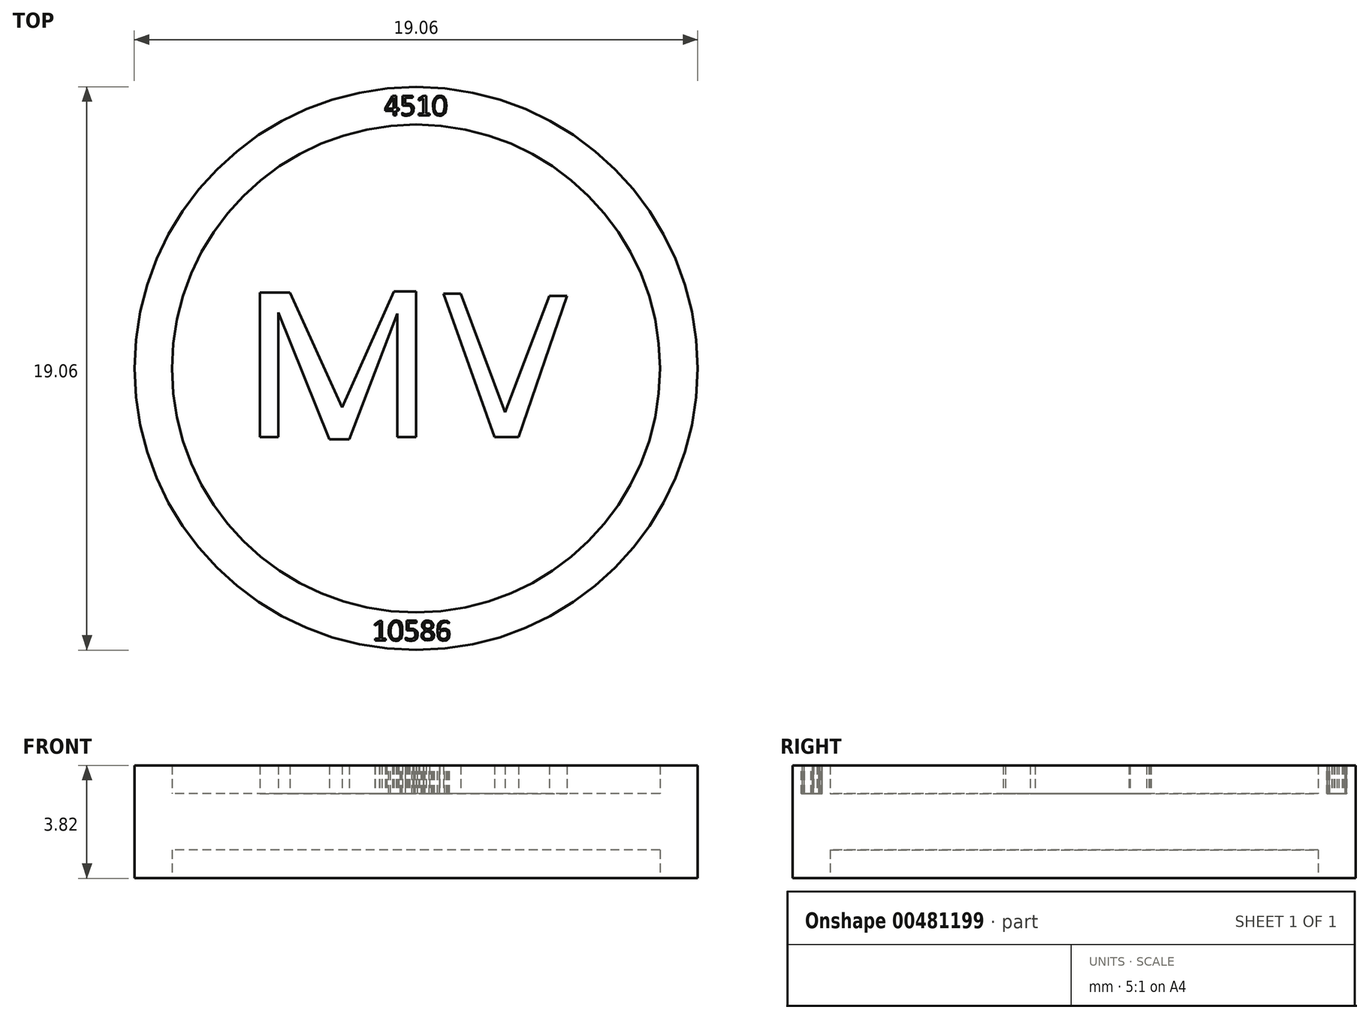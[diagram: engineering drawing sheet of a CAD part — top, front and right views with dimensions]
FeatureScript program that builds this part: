
annotation { "Feature Type Name" : "Feature", "Feature Type Description" : "" }
export const myFeature = defineFeature(function(context is Context, id is Id, definition is map)
    precondition{}
    {
        {
            var Q0;
            Q0=qCreatedBy(makeId("Top.planeOp"),FACE);
            var sketch = newSketch(context, id + "F0", { "sketchPlane" : qUnion([Q0])});
            skCircle(sketch, "E0", {"center": v(0, 0) * mm, "radius": 9.53 * mm});
            skCircle(sketch, "E1", {"center": v(0, 0) * mm, "radius": 8.26 * mm});
            skLineSegment(sketch, "E2", {"start": v(-5.28, -2.32) * mm, "end": v(-4.66, -2.32) * mm});
            skLineSegment(sketch, "E3", {"start": v(-4.66, -2.32) * mm, "end": v(-4.66, 1.9) * mm});
            skLineSegment(sketch, "E4", {"start": v(-4.66, 1.9) * mm, "end": v(-2.94, -2.39) * mm});
            skLineSegment(sketch, "E5", {"start": v(-2.94, -2.39) * mm, "end": v(-2.25, -2.39) * mm});
            skLineSegment(sketch, "E6", {"start": v(-2.25, -2.39) * mm, "end": v(-0.64, 1.86) * mm});
            skLineSegment(sketch, "E7", {"start": v(-0.64, 1.86) * mm, "end": v(-0.64, -2.32) * mm});
            skLineSegment(sketch, "E8", {"start": v(-0.64, -2.32) * mm, "end": v(0, -2.32) * mm});
            skLineSegment(sketch, "E9", {"start": v(0, -2.32) * mm, "end": v(0, 2.61) * mm});
            skLineSegment(sketch, "E10", {"start": v(0, 2.61) * mm, "end": v(-0.74, 2.61) * mm});
            skLineSegment(sketch, "E11", {"start": v(-0.74, 2.61) * mm, "end": v(-2.5, -1.31) * mm});
            skLineSegment(sketch, "E12", {"start": v(-2.5, -1.31) * mm, "end": v(-4.27, 2.57) * mm});
            skLineSegment(sketch, "E13", {"start": v(-4.27, 2.57) * mm, "end": v(-5.1, 2.57) * mm});
            skLineSegment(sketch, "E14", {"start": v(-5.28, -2.32) * mm, "end": v(-5.28, 2.57) * mm});
            skLineSegment(sketch, "E15", {"start": v(-5.28, 2.57) * mm, "end": v(-5.1, 2.57) * mm});
            skLineSegment(sketch, "E16", {"start": v(0.93, 2.53) * mm, "end": v(1.52, 2.53) * mm});
            skLineSegment(sketch, "E17", {"start": v(1.52, 2.53) * mm, "end": v(3.02, -1.48) * mm});
            skLineSegment(sketch, "E18", {"start": v(3.02, -1.48) * mm, "end": v(4.51, 2.46) * mm});
            skLineSegment(sketch, "E19", {"start": v(4.51, 2.46) * mm, "end": v(5.1, 2.46) * mm});
            skLineSegment(sketch, "E20", {"start": v(5.1, 2.46) * mm, "end": v(3.47, -2.32) * mm});
            skLineSegment(sketch, "E21", {"start": v(3.47, -2.32) * mm, "end": v(2.65, -2.32) * mm});
            skLineSegment(sketch, "E22", {"start": v(2.65, -2.32) * mm, "end": v(0.93, 2.53) * mm});
            skLineSegment(sketch, "E23", {"start": v(-0.8, 9.23) * mm, "end": v(-0.67, 9.23) * mm});
            skLineSegment(sketch, "E24", {"start": v(-0.67, 9.23) * mm, "end": v(-0.67, 8.8) * mm});
            skLineSegment(sketch, "E25", {"start": v(-0.67, 8.8) * mm, "end": v(-0.59, 8.8) * mm});
            skLineSegment(sketch, "E26", {"start": v(-0.59, 8.8) * mm, "end": v(-0.59, 8.73) * mm});
            skLineSegment(sketch, "E27", {"start": v(-0.59, 8.73) * mm, "end": v(-0.67, 8.73) * mm});
            skLineSegment(sketch, "E28", {"start": v(-0.67, 8.73) * mm, "end": v(-0.67, 8.56) * mm});
            skLineSegment(sketch, "E29", {"start": v(-0.67, 8.56) * mm, "end": v(-0.75, 8.56) * mm});
            skLineSegment(sketch, "E30", {"start": v(-0.75, 8.56) * mm, "end": v(-0.75, 8.72) * mm});
            skLineSegment(sketch, "E31", {"start": v(-0.75, 8.72) * mm, "end": v(-1.04, 8.72) * mm});
            skLineSegment(sketch, "E32", {"start": v(-1.04, 8.72) * mm, "end": v(-1.04, 8.8) * mm});
            skLineSegment(sketch, "E33", {"start": v(-1.04, 8.8) * mm, "end": v(-0.8, 9.23) * mm});
            skLineSegment(sketch, "E34", {"start": v(-0.45, 9.23) * mm, "end": v(-0.45, 8.9) * mm});
            skLineSegment(sketch, "E35", {"start": v(-0.45, 8.9) * mm, "end": v(-0.27, 8.9) * mm});
            skLineSegment(sketch, "E36", {"start": v(-0.45, 9.23) * mm, "end": v(-0.12, 9.23) * mm});
            skLineSegment(sketch, "E37", {"start": v(-0.12, 9.23) * mm, "end": v(-0.12, 9.16) * mm});
            skLineSegment(sketch, "E38", {"start": v(-0.12, 9.16) * mm, "end": v(-0.37, 9.16) * mm});
            skLineSegment(sketch, "E39", {"start": v(-0.37, 9.16) * mm, "end": v(-0.37, 8.96) * mm});
            skLineSegment(sketch, "E40", {"start": v(-0.37, 8.96) * mm, "end": v(-0.21, 8.96) * mm});
            skFitSpline(sketch, "E41", {"points": [v(-0.27, 8.9) * mm, v(-0.2, 8.88) * mm, v(-0.15, 8.81) * mm, v(-0.16, 8.67) * mm, v(-0.27, 8.61) * mm, v(-0.41, 8.62) * mm, v(-0.46, 8.65) * mm, v(-0.47, 8.62) * mm, v(-0.43, 8.57) * mm, v(-0.24, 8.56) * mm, v(-0.17, 8.59) * mm, v(-0.13, 8.62) * mm, v(-0.08, 8.74) * mm, v(-0.1, 8.88) * mm, v(-0.21, 8.96) * mm], "startDerivative": vector(0.63, -0.29) * mm, "endDerivative": vector(-1.44, 0.73) * mm});
            skLineSegment(sketch, "E42", {"start": v(0.11, 9.07) * mm, "end": v(0.25, 9.14) * mm});
            skLineSegment(sketch, "E43", {"start": v(0.25, 9.14) * mm, "end": v(0.25, 8.62) * mm});
            skLineSegment(sketch, "E44", {"start": v(0.25, 8.62) * mm, "end": v(0.1, 8.62) * mm});
            skLineSegment(sketch, "E45", {"start": v(0.1, 8.62) * mm, "end": v(0.1, 8.56) * mm});
            skLineSegment(sketch, "E46", {"start": v(0.1, 8.56) * mm, "end": v(0.46, 8.56) * mm});
            skLineSegment(sketch, "E47", {"start": v(0.46, 8.56) * mm, "end": v(0.46, 8.62) * mm});
            skLineSegment(sketch, "E48", {"start": v(0.46, 8.62) * mm, "end": v(0.34, 8.62) * mm});
            skLineSegment(sketch, "E49", {"start": v(0.34, 8.62) * mm, "end": v(0.34, 9.23) * mm});
            skLineSegment(sketch, "E50", {"start": v(0.34, 9.23) * mm, "end": v(0.26, 9.23) * mm});
            skLineSegment(sketch, "E51", {"start": v(0.26, 9.23) * mm, "end": v(0.1, 9.12) * mm});
            skLineSegment(sketch, "E52", {"start": v(0.1, 9.12) * mm, "end": v(0.1, 9.07) * mm});
            skLineSegment(sketch, "E53", {"start": v(0.1, 9.07) * mm, "end": v(0.11, 9.07) * mm});
            skFitSpline(sketch, "E54", {"points": [v(0.8, 9.17) * mm, v(0.87, 9.17) * mm, v(0.93, 9.09) * mm, v(0.96, 8.96) * mm, v(0.96, 8.8) * mm, v(0.94, 8.68) * mm, v(0.88, 8.62) * mm, v(0.77, 8.61) * mm, v(0.7, 8.63) * mm, v(0.64, 8.75) * mm, v(0.64, 9.01) * mm, v(0.7, 9.13) * mm, v(0.8, 9.17) * mm], "startDerivative": vector(1.02, 0.3) * mm, "endDerivative": vector(1.6, 0.29) * mm});
            skFitSpline(sketch, "E55", {"points": [v(0.8, 9.17) * mm, v(0.8, 9.17) * mm], "startDerivative": vector(0, 0) * mm, "endDerivative": vector(0, 0) * mm});
            skFitSpline(sketch, "E56", {"points": [v(0.8, 9.23) * mm, v(0.9, 9.21) * mm, v(0.98, 9.12) * mm, v(1.02, 8.97) * mm, v(1.01, 8.72) * mm, v(0.94, 8.61) * mm, v(0.85, 8.55) * mm, v(0.7, 8.57) * mm, v(0.6, 8.7) * mm, v(0.57, 8.93) * mm, v(0.62, 9.1) * mm, v(0.72, 9.2) * mm, v(0.8, 9.23) * mm]});
            skLineSegment(sketch, "E57", {"start": v(-0.76, 9.16) * mm, "end": v(-0.76, 8.8) * mm});
            skLineSegment(sketch, "E58", {"start": v(-0.76, 8.8) * mm, "end": v(-1, 8.8) * mm});
            skLineSegment(sketch, "E59", {"start": v(-1, 8.8) * mm, "end": v(-1, 8.82) * mm});
            skLineSegment(sketch, "E60", {"start": v(-1, 8.82) * mm, "end": v(-0.76, 9.16) * mm});
            skLineSegment(sketch, "E61", {"start": v(-1.24, -8.55) * mm, "end": v(-1.4, -8.65) * mm});
            skLineSegment(sketch, "E62", {"start": v(-1.4, -8.65) * mm, "end": v(-1.4, -8.7) * mm});
            skLineSegment(sketch, "E63", {"start": v(-1.4, -8.7) * mm, "end": v(-1.24, -8.6) * mm});
            skLineSegment(sketch, "E64", {"start": v(-1.24, -8.6) * mm, "end": v(-1.24, -9.14) * mm});
            skLineSegment(sketch, "E65", {"start": v(-1.24, -9.14) * mm, "end": v(-1.39, -9.14) * mm});
            skLineSegment(sketch, "E66", {"start": v(-1.39, -9.14) * mm, "end": v(-1.39, -9.2) * mm});
            skLineSegment(sketch, "E67", {"start": v(-1.39, -9.2) * mm, "end": v(-1.02, -9.2) * mm});
            skLineSegment(sketch, "E68", {"start": v(-1.02, -9.2) * mm, "end": v(-1.02, -9.14) * mm});
            skLineSegment(sketch, "E69", {"start": v(-1.02, -9.14) * mm, "end": v(-1.16, -9.14) * mm});
            skLineSegment(sketch, "E70", {"start": v(-1.16, -9.14) * mm, "end": v(-1.16, -8.54) * mm});
            skLineSegment(sketch, "E71", {"start": v(-1.16, -8.54) * mm, "end": v(-1.24, -8.55) * mm});
            skFitSpline(sketch, "E72", {"points": [v(-0.7, -8.59) * mm, v(-0.62, -8.6) * mm, v(-0.56, -8.69) * mm, v(-0.55, -9.07) * mm, v(-0.63, -9.14) * mm, v(-0.76, -9.15) * mm, v(-0.85, -8.99) * mm, v(-0.83, -8.7) * mm, v(-0.7, -8.59) * mm]});
            skFitSpline(sketch, "E73", {"points": [v(-0.73, -8.53) * mm, v(-0.6, -8.53) * mm, v(-0.5, -8.64) * mm, v(-0.47, -8.84) * mm, v(-0.47, -9.04) * mm, v(-0.54, -9.15) * mm, v(-0.63, -9.21) * mm, v(-0.79, -9.2) * mm, v(-0.9, -9.01) * mm, v(-0.91, -8.75) * mm, v(-0.82, -8.59) * mm, v(-0.73, -8.53) * mm]});
            skLineSegment(sketch, "E74", {"start": v(-0.31, -8.53) * mm, "end": v(0.02, -8.53) * mm});
            skLineSegment(sketch, "E75", {"start": v(0.02, -8.53) * mm, "end": v(0.02, -8.6) * mm});
            skLineSegment(sketch, "E76", {"start": v(0.02, -8.6) * mm, "end": v(-0.25, -8.6) * mm});
            skLineSegment(sketch, "E77", {"start": v(-0.25, -8.6) * mm, "end": v(-0.25, -8.81) * mm});
            skLineSegment(sketch, "E78", {"start": v(-0.25, -8.81) * mm, "end": v(-0.07, -8.81) * mm});
            skLineSegment(sketch, "E79", {"start": v(-0.31, -8.53) * mm, "end": v(-0.31, -8.86) * mm});
            skLineSegment(sketch, "E80", {"start": v(-0.31, -8.86) * mm, "end": v(-0.1, -8.86) * mm});
            skFitSpline(sketch, "E81", {"points": [v(-0.1, -8.86) * mm, v(-0.06, -8.9) * mm, v(-0.03, -9.05) * mm, v(-0.1, -9.13) * mm, v(-0.27, -9.15) * mm, v(-0.34, -9.11) * mm, v(-0.36, -9.15) * mm, v(-0.3, -9.2) * mm, v(-0.07, -9.2) * mm, v(0.05, -9.07) * mm, v(0.03, -8.9) * mm, v(-0.07, -8.81) * mm], "startDerivative": vector(0.84, -0.23) * mm, "endDerivative": vector(-1.4, 0.64) * mm});
            skFitSpline(sketch, "E82", {"points": [v(0.34, -8.53) * mm, v(0.46, -8.54) * mm, v(0.55, -8.6) * mm, v(0.59, -8.68) * mm, v(0.57, -8.78) * mm, v(0.45, -8.85) * mm, v(0.57, -8.93) * mm, v(0.6, -9.12) * mm, v(0.51, -9.18) * mm, v(0.46, -9.2) * mm, v(0.3, -9.2) * mm, v(0.2, -9.13) * mm, v(0.19, -8.98) * mm, v(0.3, -8.85) * mm, v(0.2, -8.74) * mm, v(0.23, -8.6) * mm, v(0.34, -8.53) * mm]});
            skFitSpline(sketch, "E83", {"points": [v(0.35, -8.6) * mm, v(0.47, -8.6) * mm, v(0.52, -8.65) * mm, v(0.52, -8.74) * mm, v(0.47, -8.8) * mm, v(0.4, -8.81) * mm, v(0.34, -8.8) * mm, v(0.29, -8.75) * mm, v(0.28, -8.66) * mm, v(0.35, -8.6) * mm]});
            skFitSpline(sketch, "E84", {"points": [v(0.4, -8.9) * mm, v(0.46, -8.92) * mm, v(0.5, -8.96) * mm, v(0.53, -9.02) * mm, v(0.52, -9.1) * mm, v(0.48, -9.15) * mm, v(0.39, -9.15) * mm, v(0.3, -9.14) * mm, v(0.25, -9.09) * mm, v(0.25, -8.98) * mm, v(0.31, -8.91) * mm, v(0.4, -8.9) * mm]});
            skFitSpline(sketch, "E85", {"points": [v(1.1, -8.63) * mm, v(1.08, -8.6) * mm, v(1, -8.59) * mm, v(0.9, -8.6) * mm, v(0.84, -8.67) * mm, v(0.8, -8.74) * mm, v(0.8, -8.84) * mm, v(0.88, -8.82) * mm, v(1.03, -8.81) * mm, v(1.12, -8.88) * mm, v(1.12, -9.11) * mm, v(1.02, -9.2) * mm, v(0.86, -9.2) * mm, v(0.75, -9.1) * mm, v(0.74, -8.73) * mm, v(0.76, -8.65) * mm, v(0.85, -8.55) * mm, v(1, -8.53) * mm, v(1.1, -8.56) * mm, v(1.12, -8.63) * mm, v(1.1, -8.63) * mm]});
            skFitSpline(sketch, "E86", {"points": [v(0.93, -8.87) * mm, v(1, -8.87) * mm, v(1.05, -8.9) * mm, v(1.07, -8.97) * mm, v(1.07, -9.06) * mm, v(1.03, -9.12) * mm, v(0.98, -9.15) * mm, v(0.88, -9.14) * mm, v(0.8, -9.1) * mm, v(0.8, -8.98) * mm, v(0.84, -8.88) * mm, v(0.93, -8.87) * mm]});
            skSolve(sketch);
        }
        {
            var Q0;
            Q0=makeQuery(id+"F0.imprint","IMPRINT",FACE,{"disambiguationData":[TD([[makeQuery(id+"F0.imprint","IMPRINT",EDGE,{"derivedFrom":sQuery(id+"F0.wireOp",EDGE,"E0")}),1.0]])]});
            var Q1;
            Q1=makeQuery(id+"F0.imprint","IMPRINT",FACE,{"disambiguationData":[TD([[makeQuery(id+"F0.imprint","IMPRINT",EDGE,{"derivedFrom":sQuery(id+"F0.wireOp",EDGE,"E72")}),-1.0]])]});
            var Q2;
            Q2=makeQuery(id+"F0.imprint","IMPRINT",FACE,{"disambiguationData":[TD([[makeQuery(id+"F0.imprint","IMPRINT",EDGE,{"derivedFrom":sQuery(id+"F0.wireOp",EDGE,"E84")}),-1.0]])]});
            var Q3;
            Q3=makeQuery(id+"F0.imprint","IMPRINT",FACE,{"disambiguationData":[TD([[makeQuery(id+"F0.imprint","IMPRINT",EDGE,{"derivedFrom":sQuery(id+"F0.wireOp",EDGE,"E83")}),-1.0]])]});
            var Q4;
            Q4=makeQuery(id+"F0.imprint","IMPRINT",FACE,{"disambiguationData":[TD([[makeQuery(id+"F0.imprint","IMPRINT",EDGE,{"derivedFrom":sQuery(id+"F0.wireOp",EDGE,"E86")}),-1.0]])]});
            var Q5;
            Q5=makeQuery(id+"F0.imprint","IMPRINT",FACE,{"disambiguationData":[TD([[makeQuery(id+"F0.imprint","IMPRINT",EDGE,{"derivedFrom":sQuery(id+"F0.wireOp",EDGE,"E57")}),-1.0]])]});
            var Q6;
            Q6=makeQuery(id+"F0.imprint","IMPRINT",FACE,{"disambiguationData":[TD([[makeQuery(id+"F0.imprint","IMPRINT",EDGE,{"derivedFrom":sQuery(id+"F0.wireOp",EDGE,"E54")}),-1.0]])]});
            extrude(context, id + "F1", {"entities" : qUnion([Q0, Q1, Q2, Q3, Q4, Q5, Q6]), "endBound" : BoundingType.SYMMETRIC, "depth" : 3.8 * mm});
        }
        {
            var Q0;
            Q0=makeQuery(id+"F0.imprint","IMPRINT",FACE,{"disambiguationData":[TD([[makeQuery(id+"F0.imprint","IMPRINT",EDGE,{"derivedFrom":sQuery(id+"F0.wireOp",EDGE,"E1")}),1.0]])]});
            var Q1;
            Q1=makeQuery(id+"F0.imprint","IMPRINT",FACE,{"disambiguationData":[TD([[makeQuery(id+"F0.imprint","IMPRINT",EDGE,{"derivedFrom":sQuery(id+"F0.wireOp",EDGE,"E2")}),1.0]])]});
            var Q2;
            Q2=makeQuery(id+"F0.imprint","IMPRINT",FACE,{"disambiguationData":[TD([[makeQuery(id+"F0.imprint","IMPRINT",EDGE,{"derivedFrom":sQuery(id+"F0.wireOp",EDGE,"E16")}),-1.0]])]});
            extrude(context, id + "F2", {"entities" : qUnion([Q0, Q1, Q2]), "operationType" : NewBodyOperationType.ADD, "endBound" : BoundingType.SYMMETRIC, "depth" : 1.9 * mm});
        }
        {
            var Q0;
            Q0=makeQuery(id+"F0.imprint","IMPRINT",FACE,{"disambiguationData":[TD([[makeQuery(id+"F0.imprint","IMPRINT",EDGE,{"derivedFrom":sQuery(id+"F0.wireOp",EDGE,"E2")}),1.0]])]});
            var Q1;
            Q1=makeQuery(id+"F0.imprint","IMPRINT",FACE,{"disambiguationData":[TD([[makeQuery(id+"F0.imprint","IMPRINT",EDGE,{"derivedFrom":sQuery(id+"F0.wireOp",EDGE,"E16")}),-1.0]])]});
            extrude(context, id + "F3", {"entities" : qUnion([Q0, Q1]), "operationType" : NewBodyOperationType.ADD, "depth" : 1.9 * mm});
        }
        {
            var Q0;
            Q0=makeQuery(id+"F0.imprint","IMPRINT",FACE,{"disambiguationData":[TD([[makeQuery(id+"F0.imprint","IMPRINT",EDGE,{"derivedFrom":sQuery(id+"F0.wireOp",EDGE,"E61")}),1.0]])]});
            var Q1;
            Q1=makeQuery(id+"F0.imprint","IMPRINT",FACE,{"disambiguationData":[TD([[makeQuery(id+"F0.imprint","IMPRINT",EDGE,{"derivedFrom":sQuery(id+"F0.wireOp",EDGE,"E72")}),1.0]])]});
            var Q2;
            Q2=makeQuery(id+"F0.imprint","IMPRINT",FACE,{"disambiguationData":[TD([[makeQuery(id+"F0.imprint","IMPRINT",EDGE,{"derivedFrom":sQuery(id+"F0.wireOp",EDGE,"E74")}),-1.0]])]});
            var Q3;
            Q3=makeQuery(id+"F0.imprint","IMPRINT",FACE,{"disambiguationData":[TD([[makeQuery(id+"F0.imprint","IMPRINT",EDGE,{"derivedFrom":sQuery(id+"F0.wireOp",EDGE,"E82")}),-1.0]])]});
            var Q4;
            Q4=makeQuery(id+"F0.imprint","IMPRINT",FACE,{"disambiguationData":[TD([[makeQuery(id+"F0.imprint","IMPRINT",EDGE,{"derivedFrom":sQuery(id+"F0.wireOp",EDGE,"E23")}),-1.0]])]});
            var Q5;
            Q5=makeQuery(id+"F0.imprint","IMPRINT",FACE,{"disambiguationData":[TD([[makeQuery(id+"F0.imprint","IMPRINT",EDGE,{"derivedFrom":sQuery(id+"F0.wireOp",EDGE,"E34")}),1.0]])]});
            var Q6;
            Q6=makeQuery(id+"F0.imprint","IMPRINT",FACE,{"disambiguationData":[TD([[makeQuery(id+"F0.imprint","IMPRINT",EDGE,{"derivedFrom":sQuery(id+"F0.wireOp",EDGE,"E42")}),1.0]])]});
            var Q7;
            Q7=makeQuery(id+"F0.imprint","IMPRINT",FACE,{"disambiguationData":[TD([[makeQuery(id+"F0.imprint","IMPRINT",EDGE,{"derivedFrom":sQuery(id+"F0.wireOp",EDGE,"E54")}),1.0]])]});
            var Q8;
            Q8=makeQuery(id+"F0.imprint","IMPRINT",FACE,{"disambiguationData":[TD([[makeQuery(id+"F0.imprint","IMPRINT",EDGE,{"derivedFrom":sQuery(id+"F0.wireOp",EDGE,"E85")}),-1.0]])]});
            extrude(context, id + "F4", {"entities" : qUnion([Q0, Q1, Q2, Q3, Q4, Q5, Q6, Q7, Q8]), "endBound" : BoundingType.SYMMETRIC, "depth" : 1.9 * mm});
        }
        {
            var Q0;
            Q0=makeQuery(id+"F4.opExtrude","CAP_FACE",FACE,{"disambiguationData":[OSD([sQuery(id+"F0.wireOp",EDGE,"E23"),sQuery(id+"F0.wireOp",EDGE,"E24"),sQuery(id+"F0.wireOp",EDGE,"E25"),sQuery(id+"F0.wireOp",EDGE,"E26"),sQuery(id+"F0.wireOp",EDGE,"E27"),sQuery(id+"F0.wireOp",EDGE,"E28"),sQuery(id+"F0.wireOp",EDGE,"E29"),sQuery(id+"F0.wireOp",EDGE,"E30"),sQuery(id+"F0.wireOp",EDGE,"E31"),sQuery(id+"F0.wireOp",EDGE,"E32"),sQuery(id+"F0.wireOp",EDGE,"E33"),sQuery(id+"F0.wireOp",EDGE,"E57"),sQuery(id+"F0.wireOp",EDGE,"E58"),sQuery(id+"F0.wireOp",EDGE,"E59"),sQuery(id+"F0.wireOp",EDGE,"E60")])],"isStart":true});
            var Q1;
            Q1=makeQuery(id+"F4.opExtrude","CAP_FACE",FACE,{"disambiguationData":[OSD([sQuery(id+"F0.wireOp",EDGE,"E34"),sQuery(id+"F0.wireOp",EDGE,"E35"),sQuery(id+"F0.wireOp",EDGE,"E36"),sQuery(id+"F0.wireOp",EDGE,"E37"),sQuery(id+"F0.wireOp",EDGE,"E38"),sQuery(id+"F0.wireOp",EDGE,"E39"),sQuery(id+"F0.wireOp",EDGE,"E40"),sQuery(id+"F0.wireOp",EDGE,"E41")])],"isStart":true});
            var Q2;
            Q2=makeQuery(id+"F4.opExtrude","CAP_FACE",FACE,{"disambiguationData":[OSD([sQuery(id+"F0.wireOp",EDGE,"E42"),sQuery(id+"F0.wireOp",EDGE,"E43"),sQuery(id+"F0.wireOp",EDGE,"E44"),sQuery(id+"F0.wireOp",EDGE,"E45"),sQuery(id+"F0.wireOp",EDGE,"E46"),sQuery(id+"F0.wireOp",EDGE,"E47"),sQuery(id+"F0.wireOp",EDGE,"E48"),sQuery(id+"F0.wireOp",EDGE,"E49"),sQuery(id+"F0.wireOp",EDGE,"E50"),sQuery(id+"F0.wireOp",EDGE,"E51"),sQuery(id+"F0.wireOp",EDGE,"E52"),sQuery(id+"F0.wireOp",EDGE,"E53")])],"isStart":true});
            var Q3;
            Q3=makeQuery(id+"F4.opExtrude","CAP_FACE",FACE,{"disambiguationData":[OSD([sQuery(id+"F0.wireOp",EDGE,"E54"),sQuery(id+"F0.wireOp",EDGE,"E55"),sQuery(id+"F0.wireOp",EDGE,"E56")])],"isStart":true});
            var Q4;
            Q4=makeQuery(id+"F4.opExtrude","CAP_FACE",FACE,{"disambiguationData":[OSD([sQuery(id+"F0.wireOp",EDGE,"E82"),sQuery(id+"F0.wireOp",EDGE,"E83"),sQuery(id+"F0.wireOp",EDGE,"E84")])],"isStart":true});
            var Q5;
            Q5=makeQuery(id+"F4.opExtrude","CAP_FACE",FACE,{"disambiguationData":[OSD([sQuery(id+"F0.wireOp",EDGE,"E74"),sQuery(id+"F0.wireOp",EDGE,"E75"),sQuery(id+"F0.wireOp",EDGE,"E76"),sQuery(id+"F0.wireOp",EDGE,"E77"),sQuery(id+"F0.wireOp",EDGE,"E78"),sQuery(id+"F0.wireOp",EDGE,"E79"),sQuery(id+"F0.wireOp",EDGE,"E80"),sQuery(id+"F0.wireOp",EDGE,"E81")])],"isStart":true});
            var Q6;
            Q6=makeQuery(id+"F4.opExtrude","CAP_FACE",FACE,{"disambiguationData":[OSD([sQuery(id+"F0.wireOp",EDGE,"E72"),sQuery(id+"F0.wireOp",EDGE,"E73")])],"isStart":true});
            var Q7;
            Q7=makeQuery(id+"F4.opExtrude","CAP_FACE",FACE,{"disambiguationData":[OSD([sQuery(id+"F0.wireOp",EDGE,"E61"),sQuery(id+"F0.wireOp",EDGE,"E62"),sQuery(id+"F0.wireOp",EDGE,"E63"),sQuery(id+"F0.wireOp",EDGE,"E64"),sQuery(id+"F0.wireOp",EDGE,"E65"),sQuery(id+"F0.wireOp",EDGE,"E66"),sQuery(id+"F0.wireOp",EDGE,"E67"),sQuery(id+"F0.wireOp",EDGE,"E68"),sQuery(id+"F0.wireOp",EDGE,"E69"),sQuery(id+"F0.wireOp",EDGE,"E70"),sQuery(id+"F0.wireOp",EDGE,"E71")])],"isStart":true});
            var Q8;
            Q8=makeQuery(id+"F4.opExtrude","CAP_FACE",FACE,{"disambiguationData":[OSD([sQuery(id+"F0.wireOp",EDGE,"E85"),sQuery(id+"F0.wireOp",EDGE,"E86")])],"isStart":true});
            extrude(context, id + "F5", {"entities" : qUnion([Q0, Q1, Q2, Q3, Q4, Q5, Q6, Q7, Q8]), "operationType" : NewBodyOperationType.ADD, "endBound" : BoundingType.SYMMETRIC, "depth" : 1.9 * mm});
        }
    });
